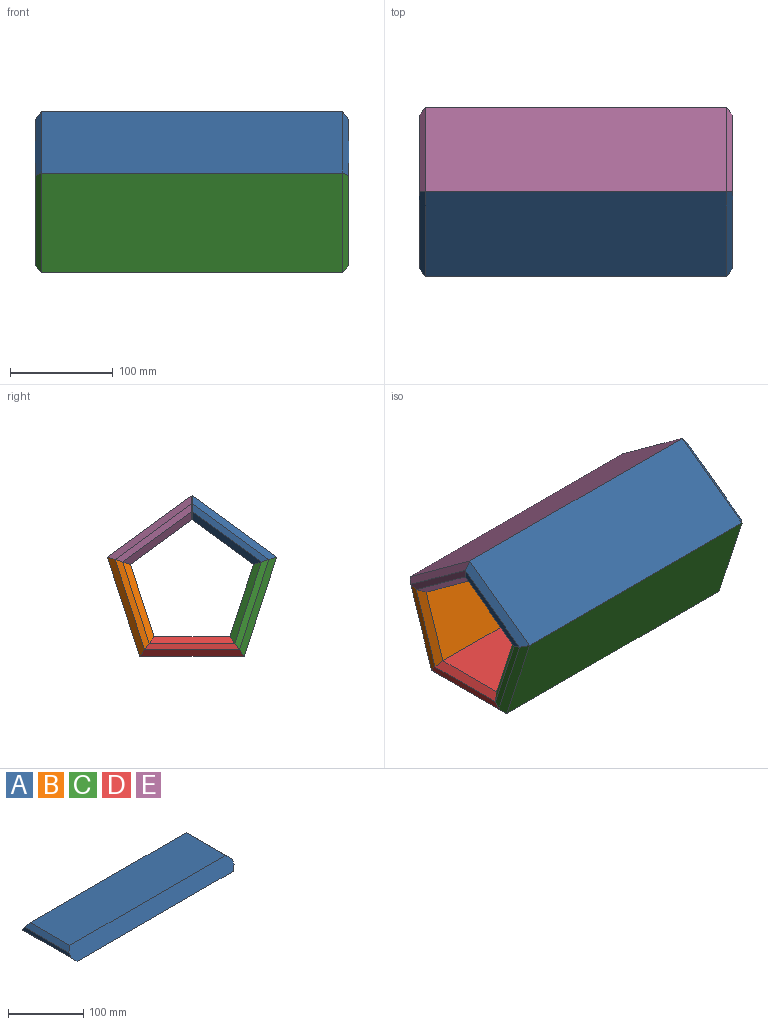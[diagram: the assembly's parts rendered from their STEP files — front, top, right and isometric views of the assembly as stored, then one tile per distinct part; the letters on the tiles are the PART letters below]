
ASSEMBLY  parts=5 mates=4
PART A: 10 faces, bbox 304.8x101.6x19.1 mm
  f0: plane 92.37x6.35mm, normal (-1,0,0), area 557.3mm2, adj f4,f5,f8,f9
  f1: plane 92.37x6.35mm, normal (1,0,0), area 557.3mm2, adj f4,f5,f6,f7
  f2: plane 292.1x73.92mm, normal (0,0,1), area 21591.7mm2, adj f4,f5,f7,f9
  f3: plane 292.1x101.6mm, normal (0,0,-1), area 29677.4mm2, adj f4,f5,f6,f8
  f4: plane 304.8x19.05mm, normal (0,0.81,0.59), area 7077.5mm2, adj f0,f1,f2,f3,f6,f7,f8,f9
  f5: plane 304.8x19.05mm, normal (0,-0.81,0.59), area 7077.5mm2, adj f0,f1,f2,f3,f6,f7,f8,f9
  f6: plane 101.6x6.35mm, normal (0.71,0,-0.71), area 871mm2, adj f1,f3,f4,f5
  f7: plane 83.15x6.35mm, normal (0.71,0,0.71), area 705.2mm2, adj f1,f2,f4,f5
  f8: plane 101.6x6.35mm, normal (-0.71,0,-0.71), area 871mm2, adj f0,f3,f4,f5
  f9: plane 83.15x6.35mm, normal (-0.71,0,0.71), area 705.2mm2, adj f0,f2,f4,f5
PART B: same geometry as A
PART C: same geometry as A
PART D: same geometry as A
PART E: same geometry as A
PLACE A rot(axis=(-1,0,0),144deg) t=(-152.4,-82.2,77.58)mm
PLACE B rot(axis=(1,0,0),72deg) t=(-152.4,82.2,77.58)mm
PLACE C rot(axis=(-1,0,0),72deg) t=(-152.4,-50.8,-19.05)mm
PLACE D t=(-152.4,50.8,-19.05)mm
PLACE E rot(axis=(1,0,0),144deg) t=(-152.4,0,137.3)mm
MATE fastened E.f5 <-> B.f4  axis (0,0.31,-0.95) through (0,71,73.94)mm
MATE fastened A.f5 <-> E.f4  axis (0,1,0) through (0,0,125.52)mm
MATE fastened D.f5 <-> C.f4  axis (0,-0.81,0.59) through (0,-43.88,-9.52)mm
MATE fastened A.f4 <-> C.f5  axis (0,-0.31,-0.95) through (0,-71,73.94)mm
